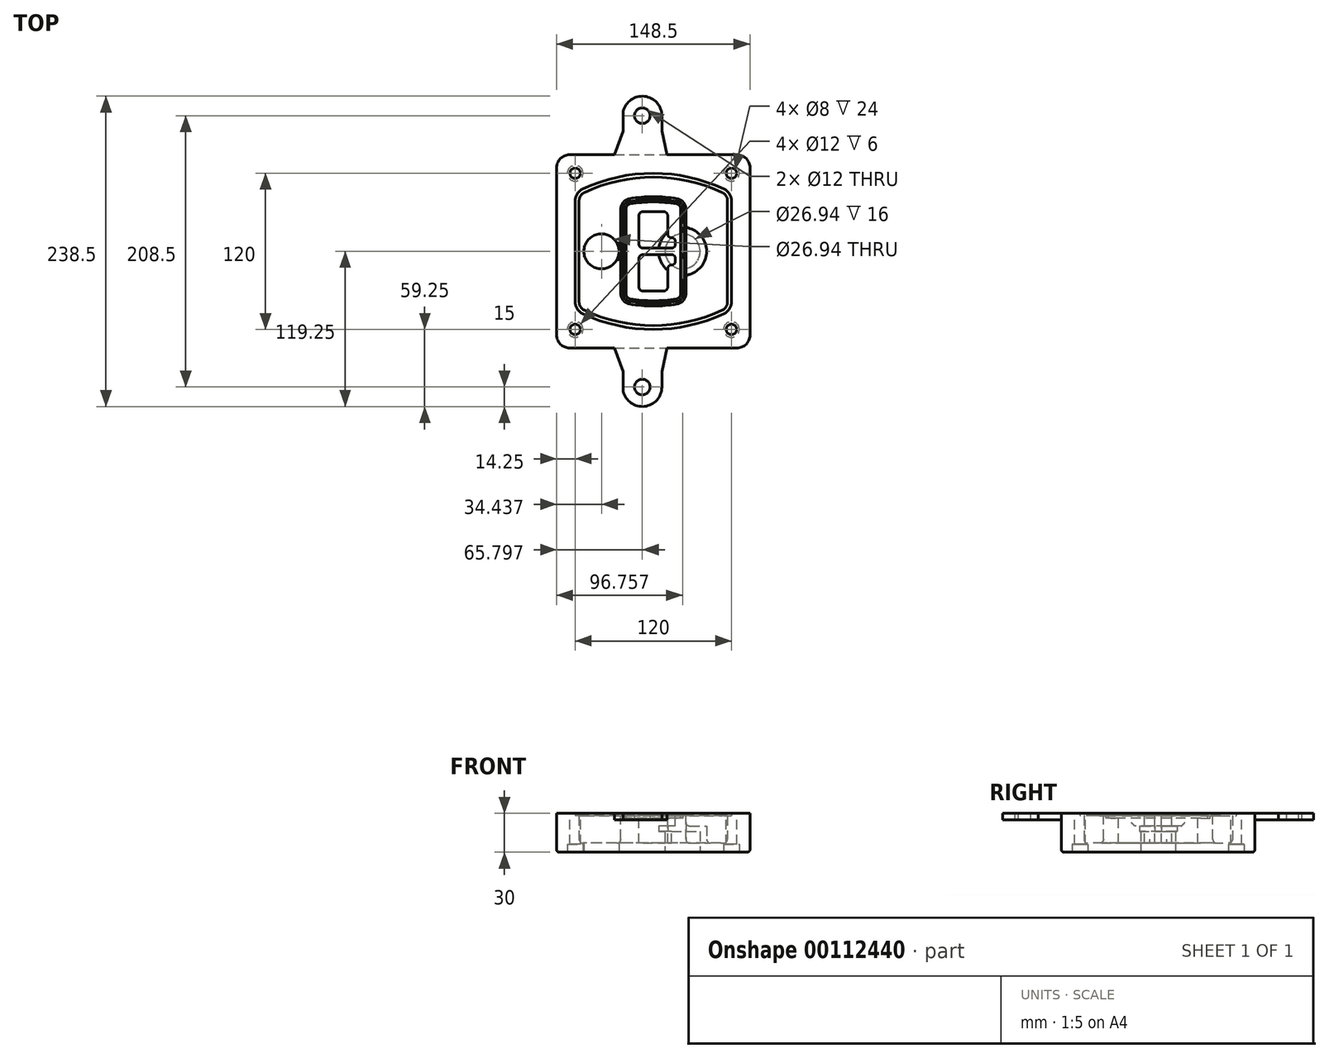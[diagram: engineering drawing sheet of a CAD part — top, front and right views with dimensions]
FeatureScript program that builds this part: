
annotation { "Feature Type Name" : "Feature", "Feature Type Description" : "" }
export const myFeature = defineFeature(function(context is Context, id is Id, definition is map)
    precondition{}
    {
        {
            var Q0;
            Q0=qCreatedBy(makeId("Top.planeOp"),FACE);
            var sketch = newSketch(context, id + "F0", { "sketchPlane" : qUnion([Q0])});
            skPoint(sketch, "E0.rect.middle", {"position": v(0, 0) * mm});
            skLineSegment(sketch, "E1.bottom", {"start": v(-64.25, -74.25) * mm, "end": v(64.25, -74.25) * mm});
            skLineSegment(sketch, "E1.top", {"start": v(-64.25, 74.25) * mm, "end": v(64.25, 74.25) * mm});
            skLineSegment(sketch, "E1.left", {"start": v(-74.25, -64.25) * mm, "end": v(-74.25, 64.25) * mm});
            skLineSegment(sketch, "E1.right", {"start": v(74.25, -64.25) * mm, "end": v(74.25, 64.25) * mm});
            skLineSegment(sketch, "E2", {"start": v(-74.25, 74.25) * mm, "end": v(74.25, -74.25) * mm, "construction": true});
            skLineSegment(sketch, "E3", {"start": v(74.25, 74.25) * mm, "end": v(-74.25, -74.25) * mm, "construction": true});
            skCircle(sketch, "E4", {"center": v(-60, 60) * mm, "radius": 4 * mm});
            skCircle(sketch, "E5", {"center": v(60, 60) * mm, "radius": 4 * mm});
            skCircle(sketch, "E6", {"center": v(60, -60) * mm, "radius": 4 * mm});
            skCircle(sketch, "E7", {"center": v(-60, -60) * mm, "radius": 4 * mm});
            skLineSegment(sketch, "E8", {"start": v(-60, 60) * mm, "end": v(60, 60) * mm, "construction": true});
            skLineSegment(sketch, "E9", {"start": v(60, 60) * mm, "end": v(60, -60) * mm, "construction": true});
            skLineSegment(sketch, "E10", {"start": v(60, -60) * mm, "end": v(-60, -60) * mm, "construction": true});
            skLineSegment(sketch, "E11", {"start": v(-60, -60) * mm, "end": v(-60, 60) * mm, "construction": true});
            skLineSegment(sketch, "E12", {"start": v(-60, 38.83) * mm, "end": v(-60, -38.83) * mm});
            skLineSegment(sketch, "E13", {"start": v(60, 38.83) * mm, "end": v(60, -38.83) * mm});
            skArc(sketch, "E14", {"start": v(54.26, 47.88) * mm, "mid": v(0, 60) * mm, "end": v(-54.26, 47.88) * mm});
            skArc(sketch, "E15", {"start": v(-54.26, -47.88) * mm, "mid": v(0, -60) * mm, "end": v(54.26, -47.88) * mm});
            skLineSegment(sketch, "E16", {"start": v(-60, 0) * mm, "end": v(60, 0) * mm, "construction": true});
            skPoint(sketch, "E17.visualSharp", {"position": v(-60, -45) * mm});
            skArc(sketch, "E17.filletArc", {"start": v(-60, -38.83) * mm, "mid": v(-58.44, -44.2) * mm, "end": v(-54.26, -47.88) * mm});
            skPoint(sketch, "E18.visualSharp", {"position": v(-60, 45) * mm});
            skArc(sketch, "E18.filletArc", {"start": v(-54.26, 47.88) * mm, "mid": v(-58.44, 44.2) * mm, "end": v(-60, 38.83) * mm});
            skPoint(sketch, "E19.visualSharp", {"position": v(60, 45) * mm});
            skArc(sketch, "E19.filletArc", {"start": v(60, 38.83) * mm, "mid": v(58.44, 44.2) * mm, "end": v(54.26, 47.88) * mm});
            skPoint(sketch, "E20.visualSharp", {"position": v(60, -45) * mm});
            skArc(sketch, "E20.filletArc", {"start": v(54.26, -47.88) * mm, "mid": v(58.44, -44.2) * mm, "end": v(60, -38.83) * mm});
            skPoint(sketch, "E21.visualSharp", {"position": v(-74.25, 74.25) * mm});
            skArc(sketch, "E21.filletArc", {"start": v(-64.25, 74.25) * mm, "mid": v(-71.32, 71.32) * mm, "end": v(-74.25, 64.25) * mm});
            skPoint(sketch, "E22.visualSharp", {"position": v(74.25, 74.25) * mm});
            skArc(sketch, "E22.filletArc", {"start": v(74.25, 64.25) * mm, "mid": v(71.32, 71.32) * mm, "end": v(64.25, 74.25) * mm});
            skPoint(sketch, "E23.visualSharp", {"position": v(74.25, -74.25) * mm});
            skArc(sketch, "E23.filletArc", {"start": v(64.25, -74.25) * mm, "mid": v(71.32, -71.32) * mm, "end": v(74.25, -64.25) * mm});
            skPoint(sketch, "E24.visualSharp", {"position": v(-74.25, -74.25) * mm});
            skArc(sketch, "E24.filletArc", {"start": v(-74.25, -64.25) * mm, "mid": v(-71.32, -71.32) * mm, "end": v(-64.25, -74.25) * mm});
            skArc(sketch, "E25.0", {"start": v(57, 38.83) * mm, "mid": v(55.9, 42.58) * mm, "end": v(52.98, 45.17) * mm});
            skLineSegment(sketch, "E25.1", {"start": v(57, 38.83) * mm, "end": v(57, -38.83) * mm});
            skArc(sketch, "E25.2", {"start": v(52.98, -45.17) * mm, "mid": v(55.9, -42.58) * mm, "end": v(57, -38.83) * mm});
            skArc(sketch, "E25.3", {"start": v(-52.98, -45.17) * mm, "mid": v(0, -57) * mm, "end": v(52.98, -45.17) * mm});
            skArc(sketch, "E25.4", {"start": v(-57, -38.83) * mm, "mid": v(-55.9, -42.58) * mm, "end": v(-52.98, -45.17) * mm});
            skArc(sketch, "E25.5", {"start": v(52.98, 45.17) * mm, "mid": v(0, 57) * mm, "end": v(-52.98, 45.17) * mm});
            skLineSegment(sketch, "E25.6", {"start": v(-57, 38.83) * mm, "end": v(-57, -38.83) * mm});
            skArc(sketch, "E25.7", {"start": v(-52.98, 45.17) * mm, "mid": v(-55.9, 42.58) * mm, "end": v(-57, 38.83) * mm});
            skArc(sketch, "E26.0", {"start": v(-55.96, 51.5) * mm, "mid": v(-61.82, 46.33) * mm, "end": v(-64, 38.83) * mm});
            skArc(sketch, "E26.1", {"start": v(55.96, 51.5) * mm, "mid": v(0, 64) * mm, "end": v(-55.96, 51.5) * mm});
            skArc(sketch, "E26.2", {"start": v(64, 38.83) * mm, "mid": v(61.82, 46.33) * mm, "end": v(55.96, 51.5) * mm});
            skLineSegment(sketch, "E26.3", {"start": v(64, 38.83) * mm, "end": v(64, -38.83) * mm});
            skArc(sketch, "E26.4", {"start": v(55.96, -51.5) * mm, "mid": v(61.82, -46.33) * mm, "end": v(64, -38.83) * mm});
            skLineSegment(sketch, "E26.5", {"start": v(-64, 38.83) * mm, "end": v(-64, -38.83) * mm});
            skArc(sketch, "E26.6", {"start": v(-55.96, -51.5) * mm, "mid": v(0, -64) * mm, "end": v(55.96, -51.5) * mm});
            skArc(sketch, "E26.7", {"start": v(-64, -38.83) * mm, "mid": v(-61.82, -46.33) * mm, "end": v(-55.96, -51.5) * mm});
            skSolve(sketch);
        }
        {
            var Q0;
            Q0=makeQuery(id+"F0.imprint","IMPRINT",FACE,{"disambiguationData":[TD([[makeQuery(id+"F0.imprint","IMPRINT",EDGE,{"derivedFrom":sQuery(id+"F0.wireOp",EDGE,"E1.bottom")}),1.0]])]});
            var Q1;
            Q1=makeQuery(id+"F0.imprint","IMPRINT",FACE,{"disambiguationData":[TD([[makeQuery(id+"F0.imprint","IMPRINT",EDGE,{"derivedFrom":sQuery(id+"F0.wireOp",EDGE,"E12")}),1.0]])]});
            var Q2;
            Q2=makeQuery(id+"F0.imprint","IMPRINT",FACE,{"disambiguationData":[TD([[makeQuery(id+"F0.imprint","IMPRINT",EDGE,{"derivedFrom":sQuery(id+"F0.wireOp",EDGE,"E25.0")}),1.0]])]});
            var Q3;
            Q3=makeQuery(id+"F0.imprint","IMPRINT",FACE,{"disambiguationData":[TD([[makeQuery(id+"F0.imprint","IMPRINT",EDGE,{"derivedFrom":sQuery(id+"F0.wireOp",EDGE,"E12")}),-1.0]])]});
            extrude(context, id + "F1", {"entities" : qUnion([Q0, Q1, Q2, Q3]), "oppositeDirection" : true, "depth" : 25 * mm});
        }
        {
            var Q0;
            Q0=makeQuery(id+"F0.imprint","IMPRINT",FACE,{"disambiguationData":[TD([[makeQuery(id+"F0.imprint","IMPRINT",EDGE,{"derivedFrom":sQuery(id+"F0.wireOp",EDGE,"E12")}),1.0]])]});
            extrude(context, id + "F2", {"entities" : qUnion([Q0]), "operationType" : NewBodyOperationType.ADD, "depth" : 3 * mm});
        }
        {
            var Q0;
            Q0=makeQuery(id+"F0.imprint","IMPRINT",FACE,{"disambiguationData":[TD([[makeQuery(id+"F0.imprint","IMPRINT",EDGE,{"derivedFrom":sQuery(id+"F0.wireOp",EDGE,"E25.0")}),1.0]])]});
            extrude(context, id + "F3", {"entities" : qUnion([Q0]), "operationType" : NewBodyOperationType.REMOVE, "oppositeDirection" : true, "depth" : 18 * mm});
        }
        {
            var Q0;
            Q0=makeQuery(id+"F2.opExtrude","CAP_FACE",FACE,{"disambiguationData":[OSD([sQuery(id+"F0.wireOp",EDGE,"E12"),sQuery(id+"F0.wireOp",EDGE,"E13"),sQuery(id+"F0.wireOp",EDGE,"E14"),sQuery(id+"F0.wireOp",EDGE,"E15"),sQuery(id+"F0.wireOp",EDGE,"E17.filletArc"),sQuery(id+"F0.wireOp",EDGE,"E18.filletArc"),sQuery(id+"F0.wireOp",EDGE,"E19.filletArc"),sQuery(id+"F0.wireOp",EDGE,"E20.filletArc"),sQuery(id+"F0.wireOp",EDGE,"E25.0"),sQuery(id+"F0.wireOp",EDGE,"E25.1"),sQuery(id+"F0.wireOp",EDGE,"E25.2"),sQuery(id+"F0.wireOp",EDGE,"E25.3"),sQuery(id+"F0.wireOp",EDGE,"E25.4"),sQuery(id+"F0.wireOp",EDGE,"E25.5"),sQuery(id+"F0.wireOp",EDGE,"E25.6"),sQuery(id+"F0.wireOp",EDGE,"E25.7")])],"isStart":false});
            var sketch = newSketch(context, id + "F4", { "sketchPlane" : qUnion([Q0])});
            skArc(sketch, "E27.0", {"start": v(-18.34, -40.45) * mm, "mid": v(0, -42) * mm, "end": v(18.34, -40.45) * mm});
            skArc(sketch, "E28.0", {"start": v(18.34, 40.45) * mm, "mid": v(0, 42) * mm, "end": v(-18.34, 40.45) * mm});
            skLineSegment(sketch, "E29", {"start": v(-25, 32.57) * mm, "end": v(-25, -32.57) * mm});
            skLineSegment(sketch, "E30", {"start": v(25, 32.57) * mm, "end": v(25, -32.57) * mm});
            skLineSegment(sketch, "E31", {"start": v(-25, 39.1) * mm, "end": v(25, 39.1) * mm, "construction": true});
            skLineSegment(sketch, "E32", {"start": v(-25, -39.1) * mm, "end": v(25, -39.1) * mm, "construction": true});
            skPoint(sketch, "E33.visualSharp", {"position": v(-25, 39.1) * mm});
            skArc(sketch, "E33.filletArc", {"start": v(-18.34, 40.45) * mm, "mid": v(-23.11, 37.73) * mm, "end": v(-25, 32.57) * mm});
            skPoint(sketch, "E34.visualSharp", {"position": v(25, 39.1) * mm});
            skArc(sketch, "E34.filletArc", {"start": v(25, 32.57) * mm, "mid": v(23.11, 37.73) * mm, "end": v(18.34, 40.45) * mm});
            skPoint(sketch, "E35.visualSharp", {"position": v(25, -39.1) * mm});
            skArc(sketch, "E35.filletArc", {"start": v(18.34, -40.45) * mm, "mid": v(23.11, -37.73) * mm, "end": v(25, -32.57) * mm});
            skPoint(sketch, "E36.visualSharp", {"position": v(-25, -39.1) * mm});
            skArc(sketch, "E36.filletArc", {"start": v(-25, -32.57) * mm, "mid": v(-23.11, -37.73) * mm, "end": v(-18.34, -40.45) * mm});
            skArc(sketch, "E37.0", {"start": v(52.98, 45.17) * mm, "mid": v(0, 57) * mm, "end": v(-52.98, 45.17) * mm});
            skArc(sketch, "E37.1", {"start": v(-52.98, 45.17) * mm, "mid": v(-55.9, 42.58) * mm, "end": v(-57, 38.83) * mm});
            skLineSegment(sketch, "E37.2", {"start": v(-57, 38.83) * mm, "end": v(-57, -38.83) * mm});
            skArc(sketch, "E37.3", {"start": v(-57, -38.83) * mm, "mid": v(-55.9, -42.58) * mm, "end": v(-52.98, -45.17) * mm});
            skArc(sketch, "E37.4", {"start": v(-52.98, -45.17) * mm, "mid": v(0, -57) * mm, "end": v(52.98, -45.17) * mm});
            skArc(sketch, "E37.5", {"start": v(52.98, -45.17) * mm, "mid": v(55.9, -42.58) * mm, "end": v(57, -38.83) * mm});
            skLineSegment(sketch, "E37.6", {"start": v(57, 38.83) * mm, "end": v(57, -38.83) * mm});
            skArc(sketch, "E37.7", {"start": v(57, 38.83) * mm, "mid": v(55.9, 42.58) * mm, "end": v(52.98, 45.17) * mm});
            skLineSegment(sketch, "E38.0", {"start": v(23, 32.57) * mm, "end": v(23, -32.57) * mm});
            skArc(sketch, "E38.1", {"start": v(18, -38.48) * mm, "mid": v(21.58, -36.44) * mm, "end": v(23, -32.57) * mm});
            skArc(sketch, "E38.2", {"start": v(-18, -38.48) * mm, "mid": v(0, -40) * mm, "end": v(18, -38.48) * mm});
            skArc(sketch, "E38.3", {"start": v(-23, -32.57) * mm, "mid": v(-21.58, -36.44) * mm, "end": v(-18, -38.48) * mm});
            skLineSegment(sketch, "E38.4", {"start": v(-23, 32.57) * mm, "end": v(-23, -32.57) * mm});
            skArc(sketch, "E38.5", {"start": v(23, 32.57) * mm, "mid": v(21.58, 36.44) * mm, "end": v(18, 38.48) * mm});
            skArc(sketch, "E38.6", {"start": v(-18, 38.48) * mm, "mid": v(-21.58, 36.44) * mm, "end": v(-23, 32.57) * mm});
            skArc(sketch, "E38.7", {"start": v(18, 38.48) * mm, "mid": v(0, 40) * mm, "end": v(-18, 38.48) * mm});
            skArc(sketch, "E39.0", {"start": v(21, 32.57) * mm, "mid": v(20.06, 35.15) * mm, "end": v(17.67, 36.5) * mm});
            skLineSegment(sketch, "E39.1", {"start": v(21, 32.57) * mm, "end": v(21, -32.57) * mm});
            skArc(sketch, "E39.2", {"start": v(17.67, -36.5) * mm, "mid": v(20.06, -35.15) * mm, "end": v(21, -32.57) * mm});
            skArc(sketch, "E39.3", {"start": v(-17.67, -36.5) * mm, "mid": v(0, -38) * mm, "end": v(17.67, -36.5) * mm});
            skArc(sketch, "E39.4", {"start": v(-21, -32.57) * mm, "mid": v(-20.06, -35.15) * mm, "end": v(-17.67, -36.5) * mm});
            skArc(sketch, "E39.5", {"start": v(17.67, 36.5) * mm, "mid": v(0, 38) * mm, "end": v(-17.67, 36.5) * mm});
            skLineSegment(sketch, "E39.6", {"start": v(-21, 32.57) * mm, "end": v(-21, -32.57) * mm});
            skArc(sketch, "E39.7", {"start": v(-17.67, 36.5) * mm, "mid": v(-20.06, 35.15) * mm, "end": v(-21, 32.57) * mm});
            skLineSegment(sketch, "E40", {"start": v(-25, 0) * mm, "end": v(25, 0) * mm, "construction": true});
            skLineSegment(sketch, "E41", {"start": v(-11, 5.5) * mm, "end": v(-11, 27.5) * mm});
            skLineSegment(sketch, "E42", {"start": v(-8, 30.5) * mm, "end": v(8, 30.5) * mm});
            skLineSegment(sketch, "E43", {"start": v(11, 27.5) * mm, "end": v(11, 13.5) * mm});
            skLineSegment(sketch, "E44", {"start": v(14, 10.5) * mm, "end": v(14, 10.5) * mm});
            skLineSegment(sketch, "E45", {"start": v(17, 7.5) * mm, "end": v(17, 5.5) * mm});
            skLineSegment(sketch, "E46", {"start": v(14, 2.5) * mm, "end": v(-8, 2.5) * mm});
            skPoint(sketch, "E47.visualSharp", {"position": v(-11, 30.5) * mm});
            skArc(sketch, "E47.filletArc", {"start": v(-8, 30.5) * mm, "mid": v(-10.12, 29.62) * mm, "end": v(-11, 27.5) * mm});
            skPoint(sketch, "E48.visualSharp", {"position": v(11, 30.5) * mm});
            skArc(sketch, "E48.filletArc", {"start": v(11, 27.5) * mm, "mid": v(10.12, 29.62) * mm, "end": v(8, 30.5) * mm});
            skPoint(sketch, "E49.visualSharp", {"position": v(11, 10.5) * mm});
            skArc(sketch, "E49.filletArc", {"start": v(11, 13.5) * mm, "mid": v(11.88, 11.38) * mm, "end": v(14, 10.5) * mm});
            skPoint(sketch, "E50.visualSharp", {"position": v(17, 10.5) * mm});
            skArc(sketch, "E50.filletArc", {"start": v(17, 7.5) * mm, "mid": v(16.12, 9.62) * mm, "end": v(14, 10.5) * mm});
            skPoint(sketch, "E51.visualSharp", {"position": v(17, 2.5) * mm});
            skArc(sketch, "E51.filletArc", {"start": v(14, 2.5) * mm, "mid": v(16.12, 3.38) * mm, "end": v(17, 5.5) * mm});
            skPoint(sketch, "E52.visualSharp", {"position": v(-11, 2.5) * mm});
            skArc(sketch, "E52.filletArc", {"start": v(-11, 5.5) * mm, "mid": v(-10.12, 3.38) * mm, "end": v(-8, 2.5) * mm});
            skLineSegment(sketch, "E53.0.MirrorCS", {"start": v(14, -2.5) * mm, "end": v(-8, -2.5) * mm});
            skArc(sketch, "E54.0.MirrorCS", {"start": v(-11, -5.5) * mm, "mid": v(-10.12, -3.38) * mm, "end": v(-8, -2.5) * mm});
            skLineSegment(sketch, "E55.0.MirrorCS", {"start": v(-11, -5.5) * mm, "end": v(-11, -27.5) * mm});
            skArc(sketch, "E56.0.MirrorCS", {"start": v(-8, -30.5) * mm, "mid": v(-10.12, -29.62) * mm, "end": v(-11, -27.5) * mm});
            skLineSegment(sketch, "E57.0.MirrorCS", {"start": v(-8, -30.5) * mm, "end": v(8, -30.5) * mm});
            skArc(sketch, "E58.0.MirrorCS", {"start": v(11, -27.5) * mm, "mid": v(10.12, -29.62) * mm, "end": v(8, -30.5) * mm});
            skLineSegment(sketch, "E59.0.MirrorCS", {"start": v(11, -27.5) * mm, "end": v(11, -13.5) * mm});
            skArc(sketch, "E60.0.MirrorCS", {"start": v(11, -13.5) * mm, "mid": v(11.88, -11.38) * mm, "end": v(14, -10.5) * mm});
            skArc(sketch, "E61.0.MirrorCS", {"start": v(17, -7.5) * mm, "mid": v(16.12, -9.62) * mm, "end": v(14, -10.5) * mm});
            skLineSegment(sketch, "E62.0.MirrorCS", {"start": v(17, -7.5) * mm, "end": v(17, -5.5) * mm});
            skArc(sketch, "E63.0.MirrorCS", {"start": v(14, -2.5) * mm, "mid": v(16.12, -3.38) * mm, "end": v(17, -5.5) * mm});
            skSolve(sketch);
        }
        {
            var Q0;
            Q0=makeQuery(id+"F4.imprint","IMPRINT",FACE,{"disambiguationData":[TD([[makeQuery(id+"F4.imprint","IMPRINT",EDGE,{"derivedFrom":sQuery(id+"F4.wireOp",EDGE,"E27.0")}),1.0]])]});
            var Q1;
            Q1=makeQuery(id+"F4.imprint","IMPRINT",FACE,{"disambiguationData":[TD([[makeQuery(id+"F4.imprint","IMPRINT",EDGE,{"derivedFrom":sQuery(id+"F4.wireOp",EDGE,"E38.0")}),-1.0]])]});
            var Q2;
            Q2=makeQuery(id+"F4.imprint","IMPRINT",FACE,{"disambiguationData":[TD([[makeQuery(id+"F4.imprint","IMPRINT",EDGE,{"derivedFrom":sQuery(id+"F4.wireOp",EDGE,"E39.0")}),1.0]])]});
            extrude(context, id + "F5", {"entities" : qUnion([Q0, Q1, Q2]), "operationType" : NewBodyOperationType.ADD, "endBound" : BoundingType.UP_TO_NEXT, "oppositeDirection" : true, "depth" : 25 * mm});
        }
        {
            var Q0;
            Q0=makeQuery(id+"F4.imprint","IMPRINT",FACE,{"disambiguationData":[TD([[makeQuery(id+"F4.imprint","IMPRINT",EDGE,{"derivedFrom":sQuery(id+"F4.wireOp",EDGE,"E38.0")}),-1.0]])]});
            extrude(context, id + "F6", {"entities" : qUnion([Q0]), "operationType" : NewBodyOperationType.REMOVE, "oppositeDirection" : true, "depth" : 2 * mm});
        }
        {
            var Q0;
            Q0=makeQuery(id+"F1.opExtrude","CAP_FACE",FACE,{"disambiguationData":[OSD([sQuery(id+"F0.wireOp",EDGE,"E1.bottom"),sQuery(id+"F0.wireOp",EDGE,"E1.top"),sQuery(id+"F0.wireOp",EDGE,"E1.left"),sQuery(id+"F0.wireOp",EDGE,"E1.right"),sQuery(id+"F0.wireOp",EDGE,"E4"),sQuery(id+"F0.wireOp",EDGE,"E5"),sQuery(id+"F0.wireOp",EDGE,"E6"),sQuery(id+"F0.wireOp",EDGE,"E7"),sQuery(id+"F0.wireOp",EDGE,"E21.filletArc"),sQuery(id+"F0.wireOp",EDGE,"E22.filletArc"),sQuery(id+"F0.wireOp",EDGE,"E23.filletArc"),sQuery(id+"F0.wireOp",EDGE,"E24.filletArc")])],"isStart":false});
            var sketch = newSketch(context, id + "F7", { "sketchPlane" : qUnion([Q0])});
            skCircle(sketch, "E64", {"center": v(22.5, 0) * mm, "radius": 13.47 * mm});
            skCircle(sketch, "E65", {"center": v(-39.81, 0) * mm, "radius": 13.47 * mm});
            skLineSegment(sketch, "E66", {"start": v(74.25, 0) * mm, "end": v(-74.25, 0) * mm});
            skCircle(sketch, "E67", {"center": v(22.5, 0) * mm, "radius": 18.47 * mm});
            skCircle(sketch, "E68", {"center": v(60, -60) * mm, "radius": 6 * mm});
            skCircle(sketch, "E69", {"center": v(-60, -60) * mm, "radius": 6 * mm});
            skCircle(sketch, "E70", {"center": v(-60, 60) * mm, "radius": 6 * mm});
            skCircle(sketch, "E71", {"center": v(60, 60) * mm, "radius": 6 * mm});
            skSolve(sketch);
        }
        {
            var Q0;
            {var subQ1=sQuery(id+"F7.wireOp",EDGE,"E66");var subQ4=sQuery(id+"F7.wireOp",EDGE,"E64");var subQ6=makeQuery(id+"F7.imprint","INTERSECT",VERTEX,{"disambiguationData":[OD(0.0)],"derivedFrom":[subQ4,subQ1]});Q0=makeQuery(id+"F7.imprint","IMPRINT",FACE,{"disambiguationData":[TD([[makeQuery(id+"F7.imprint","IMPRINT",EDGE,{"disambiguationData":[TD([[subQ6,-1.0]])],"derivedFrom":subQ4}),-1.0]])]});}
            var Q1;
            {var subQ0=sQuery(id+"F7.wireOp",EDGE,"E66");var subQ1=sQuery(id+"F7.wireOp",EDGE,"E64");var subQ3=makeQuery(id+"F7.imprint","INTERSECT",VERTEX,{"disambiguationData":[OD(0.0)],"derivedFrom":[subQ1,subQ0]});Q1=makeQuery(id+"F7.imprint","IMPRINT",FACE,{"disambiguationData":[TD([[makeQuery(id+"F7.imprint","IMPRINT",EDGE,{"disambiguationData":[TD([[subQ3,-1.0]])],"derivedFrom":subQ1}),1.0]])]});}
            var Q2;
            {var subQ0=sQuery(id+"F7.wireOp",EDGE,"E66");var subQ1=sQuery(id+"F7.wireOp",EDGE,"E64");var subQ3=makeQuery(id+"F7.imprint","INTERSECT",VERTEX,{"disambiguationData":[OD(0.0)],"derivedFrom":[subQ1,subQ0]});Q2=makeQuery(id+"F7.imprint","IMPRINT",FACE,{"disambiguationData":[TD([[makeQuery(id+"F7.imprint","IMPRINT",EDGE,{"disambiguationData":[TD([[subQ3,1.0]])],"derivedFrom":subQ1}),1.0]])]});}
            var Q3;
            {var subQ1=sQuery(id+"F7.wireOp",EDGE,"E66");var subQ4=sQuery(id+"F7.wireOp",EDGE,"E64");var subQ6=makeQuery(id+"F7.imprint","INTERSECT",VERTEX,{"disambiguationData":[OD(0.0)],"derivedFrom":[subQ4,subQ1]});Q3=makeQuery(id+"F7.imprint","IMPRINT",FACE,{"disambiguationData":[TD([[makeQuery(id+"F7.imprint","IMPRINT",EDGE,{"disambiguationData":[TD([[subQ6,1.0]])],"derivedFrom":subQ4}),-1.0]])]});}
            extrude(context, id + "F8", {"entities" : qUnion([Q0, Q1, Q2, Q3]), "operationType" : NewBodyOperationType.ADD, "oppositeDirection" : true, "depth" : 20 * mm});
        }
        {
            var Q0;
            {var subQ0=sQuery(id+"F7.wireOp",EDGE,"E66");var subQ1=sQuery(id+"F7.wireOp",EDGE,"E64");var subQ3=makeQuery(id+"F7.imprint","INTERSECT",VERTEX,{"disambiguationData":[OD(0.0)],"derivedFrom":[subQ1,subQ0]});Q0=makeQuery(id+"F7.imprint","IMPRINT",FACE,{"disambiguationData":[TD([[makeQuery(id+"F7.imprint","IMPRINT",EDGE,{"disambiguationData":[TD([[subQ3,-1.0]])],"derivedFrom":subQ1}),1.0]])]});}
            var Q1;
            {var subQ0=sQuery(id+"F7.wireOp",EDGE,"E66");var subQ1=sQuery(id+"F7.wireOp",EDGE,"E64");var subQ3=makeQuery(id+"F7.imprint","INTERSECT",VERTEX,{"disambiguationData":[OD(0.0)],"derivedFrom":[subQ1,subQ0]});Q1=makeQuery(id+"F7.imprint","IMPRINT",FACE,{"disambiguationData":[TD([[makeQuery(id+"F7.imprint","IMPRINT",EDGE,{"disambiguationData":[TD([[subQ3,1.0]])],"derivedFrom":subQ1}),1.0]])]});}
            extrude(context, id + "F9", {"entities" : qUnion([Q0, Q1]), "operationType" : NewBodyOperationType.REMOVE, "oppositeDirection" : true, "depth" : 16 * mm});
        }
        {
            var Q0;
            {var subQ0=sQuery(id+"F7.wireOp",EDGE,"E66");var subQ1=sQuery(id+"F7.wireOp",EDGE,"E65");var subQ3=makeQuery(id+"F7.imprint","INTERSECT",VERTEX,{"disambiguationData":[OD(0.0)],"derivedFrom":[subQ1,subQ0]});Q0=makeQuery(id+"F7.imprint","IMPRINT",FACE,{"disambiguationData":[TD([[makeQuery(id+"F7.imprint","IMPRINT",EDGE,{"disambiguationData":[TD([[subQ3,-1.0]])],"derivedFrom":subQ1}),1.0]])]});}
            var Q1;
            {var subQ0=sQuery(id+"F7.wireOp",EDGE,"E66");var subQ1=sQuery(id+"F7.wireOp",EDGE,"E65");var subQ3=makeQuery(id+"F7.imprint","INTERSECT",VERTEX,{"disambiguationData":[OD(0.0)],"derivedFrom":[subQ1,subQ0]});Q1=makeQuery(id+"F7.imprint","IMPRINT",FACE,{"disambiguationData":[TD([[makeQuery(id+"F7.imprint","IMPRINT",EDGE,{"disambiguationData":[TD([[subQ3,1.0]])],"derivedFrom":subQ1}),1.0]])]});}
            extrude(context, id + "F10", {"entities" : qUnion([Q0, Q1]), "operationType" : NewBodyOperationType.REMOVE, "oppositeDirection" : true, "depth" : 25 * mm});
        }
        {
            var Q0;
            Q0=makeQuery(id+"F7.imprint","IMPRINT",FACE,{"disambiguationData":[TD([[makeQuery(id+"F7.imprint","IMPRINT",EDGE,{"derivedFrom":sQuery(id+"F7.wireOp",EDGE,"E68")}),1.0]])]});
            var Q1;
            Q1=makeQuery(id+"F7.imprint","IMPRINT",FACE,{"disambiguationData":[TD([[makeQuery(id+"F7.imprint","IMPRINT",EDGE,{"derivedFrom":makeQuery(id+"F1.opExtrude","CAP_EDGE",EDGE,{"disambiguationData":[OSD([sQuery(id+"F0.wireOp",EDGE,"E5")])],"isStart":false})}),-1.0]])]});
            var Q2;
            Q2=makeQuery(id+"F7.imprint","IMPRINT",FACE,{"disambiguationData":[TD([[makeQuery(id+"F7.imprint","IMPRINT",EDGE,{"derivedFrom":sQuery(id+"F7.wireOp",EDGE,"E69")}),1.0]])]});
            var Q3;
            Q3=makeQuery(id+"F7.imprint","IMPRINT",FACE,{"disambiguationData":[TD([[makeQuery(id+"F7.imprint","IMPRINT",EDGE,{"derivedFrom":makeQuery(id+"F1.opExtrude","CAP_EDGE",EDGE,{"disambiguationData":[OSD([sQuery(id+"F0.wireOp",EDGE,"E4")])],"isStart":false})}),-1.0]])]});
            var Q4;
            Q4=makeQuery(id+"F7.imprint","IMPRINT",FACE,{"disambiguationData":[TD([[makeQuery(id+"F7.imprint","IMPRINT",EDGE,{"derivedFrom":sQuery(id+"F7.wireOp",EDGE,"E70")}),1.0]])]});
            var Q5;
            Q5=makeQuery(id+"F7.imprint","IMPRINT",FACE,{"disambiguationData":[TD([[makeQuery(id+"F7.imprint","IMPRINT",EDGE,{"derivedFrom":makeQuery(id+"F1.opExtrude","CAP_EDGE",EDGE,{"disambiguationData":[OSD([sQuery(id+"F0.wireOp",EDGE,"E7")])],"isStart":false})}),-1.0]])]});
            var Q6;
            Q6=makeQuery(id+"F7.imprint","IMPRINT",FACE,{"disambiguationData":[TD([[makeQuery(id+"F7.imprint","IMPRINT",EDGE,{"derivedFrom":sQuery(id+"F7.wireOp",EDGE,"E71")}),1.0]])]});
            var Q7;
            Q7=makeQuery(id+"F7.imprint","IMPRINT",FACE,{"disambiguationData":[TD([[makeQuery(id+"F7.imprint","IMPRINT",EDGE,{"derivedFrom":makeQuery(id+"F1.opExtrude","CAP_EDGE",EDGE,{"disambiguationData":[OSD([sQuery(id+"F0.wireOp",EDGE,"E6")])],"isStart":false})}),-1.0]])]});
            extrude(context, id + "F11", {"entities" : qUnion([Q0, Q1, Q2, Q3, Q4, Q5, Q6, Q7]), "operationType" : NewBodyOperationType.REMOVE, "oppositeDirection" : true, "depth" : 6 * mm});
        }
        {
            var Q0;
            Q0=makeQuery(id+"F9.boolean.opBoolean","COPY",FACE,{"derivedFrom":makeQuery(id+"F9.opExtrude","CAP_FACE",FACE,{"disambiguationData":[OSD([sQuery(id+"F7.wireOp",EDGE,"E64")])],"isStart":false})});
            var sketch = newSketch(context, id + "F12", { "sketchPlane" : qUnion([Q0])});
            skArc(sketch, "E72.0", {"start": v(11, 14.45) * mm, "mid": v(6.45, 9.13) * mm, "end": v(4.2, 2.5) * mm});
            skArc(sketch, "E72.1", {"start": v(4.2, -2.5) * mm, "mid": v(6.45, -9.13) * mm, "end": v(11, -14.45) * mm});
            skLineSegment(sketch, "E73", {"start": v(4.2, -2.5) * mm, "end": v(14, -2.5) * mm});
            skLineSegment(sketch, "E74.0", {"start": v(14, 2.5) * mm, "end": v(4.2, 2.5) * mm});
            skArc(sketch, "E74.1", {"start": v(14, 2.5) * mm, "mid": v(16.12, 3.38) * mm, "end": v(17, 5.5) * mm});
            skLineSegment(sketch, "E74.2", {"start": v(17, 7.5) * mm, "end": v(17, 5.5) * mm});
            skArc(sketch, "E74.3", {"start": v(17, 7.5) * mm, "mid": v(16.12, 9.62) * mm, "end": v(14, 10.5) * mm});
            skArc(sketch, "E74.4", {"start": v(11, 13.5) * mm, "mid": v(11.88, 11.38) * mm, "end": v(14, 10.5) * mm});
            skLineSegment(sketch, "E74.5", {"start": v(11, 14.45) * mm, "end": v(11, 13.5) * mm});
            skLineSegment(sketch, "E74.7", {"start": v(14, -2.5) * mm, "end": v(4.2, -2.5) * mm});
            skArc(sketch, "E74.8", {"start": v(14, -2.5) * mm, "mid": v(16.12, -3.38) * mm, "end": v(17, -5.5) * mm});
            skLineSegment(sketch, "E74.9", {"start": v(17, -7.5) * mm, "end": v(17, -5.5) * mm});
            skArc(sketch, "E74.10", {"start": v(17, -7.5) * mm, "mid": v(16.12, -9.62) * mm, "end": v(14, -10.5) * mm});
            skArc(sketch, "E74.11", {"start": v(11, -13.5) * mm, "mid": v(11.88, -11.38) * mm, "end": v(14, -10.5) * mm});
            skLineSegment(sketch, "E74.12", {"start": v(11, -14.45) * mm, "end": v(11, -13.5) * mm});
            skPoint(sketch, "E75.orphan", {"position": v(11, -27.5) * mm});
            skPoint(sketch, "E76.orphan", {"position": v(-8, -2.5) * mm});
            skPoint(sketch, "E77.orphan", {"position": v(-8, 2.5) * mm});
            skPoint(sketch, "E78.orphan", {"position": v(11, 27.5) * mm});
            skSolve(sketch);
        }
        {
            var Q0;
            {var subQ7=sQuery(id+"F12.wireOp",EDGE,"E72.0");var subQ14=sQuery(id+"F12.wireOp",EDGE,"E72.1");var subQ16=sQuery(id+"F12.wireOp",EDGE,"E74.1");var subQ18=sQuery(id+"F12.wireOp",EDGE,"E74.8");Q0=qUnion([makeQuery(id+"F12.imprint","IMPRINT",FACE,{"disambiguationData":[TD([[makeQuery(id+"F12.imprint","IMPRINT",EDGE,{"derivedFrom":subQ7}),1.0]])]}),makeQuery(id+"F12.imprint","IMPRINT",FACE,{"disambiguationData":[TD([[makeQuery(id+"F12.imprint","IMPRINT",EDGE,{"derivedFrom":subQ14}),1.0]])]}),makeQuery(id+"F12.imprint","IMPRINT",FACE,{"disambiguationData":[TD([[makeQuery(id+"F12.imprint","IMPRINT",EDGE,{"derivedFrom":subQ16}),1.0]])]}),makeQuery(id+"F12.imprint","IMPRINT",FACE,{"disambiguationData":[TD([[makeQuery(id+"F12.imprint","IMPRINT",EDGE,{"derivedFrom":subQ18}),-1.0]])]})]);}
            var Q1;
            Q1=makeQuery(id+"F5.boolean.opBoolean","SPLIT",FACE,{"disambiguationData":[TD([makeQuery(id+"F5.opExtrude","SWEPT_FACE",FACE,{"disambiguationData":[OSD([sQuery(id+"F4.wireOp",EDGE,"E41")])]})])],"derivedFrom":makeQuery(id+"F3.boolean.opBoolean","COPY",FACE,{"derivedFrom":makeQuery(id+"F3.opExtrude","CAP_FACE",FACE,{"disambiguationData":[OSD([sQuery(id+"F0.wireOp",EDGE,"E25.0"),sQuery(id+"F0.wireOp",EDGE,"E25.1"),sQuery(id+"F0.wireOp",EDGE,"E25.2"),sQuery(id+"F0.wireOp",EDGE,"E25.3"),sQuery(id+"F0.wireOp",EDGE,"E25.4"),sQuery(id+"F0.wireOp",EDGE,"E25.5"),sQuery(id+"F0.wireOp",EDGE,"E25.6"),sQuery(id+"F0.wireOp",EDGE,"E25.7")])],"isStart":false})})});
            extrude(context, id + "F13", {"entities" : qUnion([Q0]), "operationType" : NewBodyOperationType.REMOVE, "endBound" : BoundingType.UP_TO_SURFACE, "endBoundEntityFace" : qUnion([Q1]), "depth" : 25 * mm});
        }
        {
            var Q0;
            Q0=makeQuery(id+"F3.boolean.opBoolean","COPY",EDGE,{"derivedFrom":makeQuery(id+"F3.opExtrude","CAP_EDGE",EDGE,{"disambiguationData":[OSD([sQuery(id+"F0.wireOp",EDGE,"E25.6")])],"isStart":false})});
            var Q1;
            Q1=makeQuery(id+"F8.boolean.opBoolean","INTERSECT",EDGE,{"derivedFrom":[makeQuery(id+"F5.opExtrude","SWEPT_FACE",FACE,{"disambiguationData":[OSD([sQuery(id+"F4.wireOp",EDGE,"E30")])]}),makeQuery(id+"F8.opExtrude","CAP_FACE",FACE,{"disambiguationData":[OSD([sQuery(id+"F7.wireOp",EDGE,"E67")])],"isStart":false})]});
            var Q2;
            Q2=makeQuery(id+"F8.boolean.opBoolean","INTERSECT",EDGE,{"disambiguationData":[OD(1.0)],"derivedFrom":[makeQuery(id+"F5.opExtrude","SWEPT_FACE",FACE,{"disambiguationData":[OSD([sQuery(id+"F4.wireOp",EDGE,"E30")])]}),makeQuery(id+"F8.opExtrude","SWEPT_FACE",FACE,{"disambiguationData":[OSD([sQuery(id+"F7.wireOp",EDGE,"E67")])]})]});
            var Q3;
            {var subQ0=sQuery(id+"F4.wireOp",EDGE,"E30");Q3=makeQuery(id+"F8.boolean.opBoolean","SPLIT",EDGE,{"disambiguationData":[TD([makeQuery(id+"F5.opExtrude","SWEPT_FACE",FACE,{"disambiguationData":[OSD([sQuery(id+"F4.wireOp",EDGE,"E35.filletArc")])]})])],"derivedFrom":makeQuery(id+"F5.opExtrude","CAP_EDGE",EDGE,{"disambiguationData":[OSD([subQ0])],"isStart":false})});}
            var Q4;
            {var subQ0=sQuery(id+"F0.wireOp",EDGE,"E25.7");var subQ1=sQuery(id+"F0.wireOp",EDGE,"E25.1");var subQ2=sQuery(id+"F0.wireOp",EDGE,"E25.6");var subQ3=sQuery(id+"F0.wireOp",EDGE,"E25.5");var subQ4=sQuery(id+"F0.wireOp",EDGE,"E25.4");var subQ5=sQuery(id+"F0.wireOp",EDGE,"E25.0");var subQ6=sQuery(id+"F0.wireOp",EDGE,"E25.2");var subQ7=sQuery(id+"F0.wireOp",EDGE,"E25.3");Q4=makeQuery(id+"F8.boolean.opBoolean","INTERSECT",EDGE,{"derivedFrom":[makeQuery(id+"F5.boolean.opBoolean","SPLIT",FACE,{"disambiguationData":[TD([makeQuery(id+"F2.opExtrude","SWEPT_FACE",FACE,{"disambiguationData":[OSD([subQ5])]})])],"derivedFrom":makeQuery(id+"F3.boolean.opBoolean","COPY",FACE,{"derivedFrom":makeQuery(id+"F3.opExtrude","CAP_FACE",FACE,{"disambiguationData":[OSD([subQ5,subQ1,subQ6,subQ7,subQ4,subQ3,subQ2,subQ0])],"isStart":false})})}),makeQuery(id+"F8.opExtrude","SWEPT_FACE",FACE,{"disambiguationData":[OSD([sQuery(id+"F7.wireOp",EDGE,"E67")])]})]});}
            var Q5;
            Q5=makeQuery(id+"F8.boolean.opBoolean","INTERSECT",EDGE,{"disambiguationData":[OD(0.0)],"derivedFrom":[makeQuery(id+"F5.opExtrude","SWEPT_FACE",FACE,{"disambiguationData":[OSD([sQuery(id+"F4.wireOp",EDGE,"E30")])]}),makeQuery(id+"F8.opExtrude","SWEPT_FACE",FACE,{"disambiguationData":[OSD([sQuery(id+"F7.wireOp",EDGE,"E67")])]})]});
            fillet(context, id + "F14", {"entities" : qUnion([Q0, Q1, Q2, Q3, Q4, Q5]), "radius" : 3 * mm, "tangentPropagation" : true, "allowEdgeOverflow" : false});
        }
        {
            var Q0;
            Q0=makeQuery(id+"F1.opExtrude","CAP_EDGE",EDGE,{"disambiguationData":[OSD([sQuery(id+"F0.wireOp",EDGE,"E1.bottom")])],"isStart":false});
            fillet(context, id + "F15", {"entities" : qUnion([Q0]), "radius" : 2 * mm, "tangentPropagation" : true, "allowEdgeOverflow" : false});
        }
        {
            var Q0;
            {var subQ0=sQuery(id+"F0.wireOp",EDGE,"E22.filletArc");var subQ1=sQuery(id+"F0.wireOp",EDGE,"E7");var subQ2=sQuery(id+"F0.wireOp",EDGE,"E6");var subQ3=sQuery(id+"F0.wireOp",EDGE,"E5");var subQ4=sQuery(id+"F0.wireOp",EDGE,"E4");var subQ5=sQuery(id+"F0.wireOp",EDGE,"E1.bottom");var subQ6=sQuery(id+"F0.wireOp",EDGE,"E21.filletArc");var subQ7=sQuery(id+"F0.wireOp",EDGE,"E1.top");var subQ8=sQuery(id+"F0.wireOp",EDGE,"E1.left");var subQ9=sQuery(id+"F0.wireOp",EDGE,"E1.right");var subQ10=sQuery(id+"F0.wireOp",EDGE,"E23.filletArc");var subQ11=sQuery(id+"F0.wireOp",EDGE,"E24.filletArc");Q0=makeQuery(id+"F2.boolean.opBoolean","SPLIT",FACE,{"disambiguationData":[TD([makeQuery(id+"F1.opExtrude","SWEPT_FACE",FACE,{"disambiguationData":[OSD([subQ5])]})])],"derivedFrom":makeQuery(id+"F1.opExtrude","CAP_FACE",FACE,{"disambiguationData":[OSD([subQ5,subQ7,subQ8,subQ9,subQ4,subQ3,subQ2,subQ1,subQ6,subQ0,subQ10,subQ11])],"isStart":true})});}
            var sketch = newSketch(context, id + "F16", { "sketchPlane" : qUnion([Q0])});
            skLineSegment(sketch, "E79", {"start": v(-29.78, 74.25) * mm, "end": v(-23.06, 92.25) * mm});
            skLineSegment(sketch, "E80", {"start": v(-23.06, 92.25) * mm, "end": v(-23.06, 107.66) * mm});
            skLineSegment(sketch, "E81", {"start": v(10.4, 74.25) * mm, "end": v(6.55, 92.25) * mm});
            skLineSegment(sketch, "E82", {"start": v(6.55, 92.25) * mm, "end": v(6.55, 104.25) * mm});
            skArc(sketch, "E83", {"start": v(6.55, 104.25) * mm, "mid": v(-6.74, 119.15) * mm, "end": v(-23.06, 107.66) * mm});
            skCircle(sketch, "E84", {"center": v(-8.45, 104.25) * mm, "radius": 6 * mm});
            skLineSegment(sketch, "E85", {"start": v(-74.25, 0) * mm, "end": v(74.25, 0) * mm});
            skLineSegment(sketch, "E86.MirrorCS", {"start": v(-29.78, -74.25) * mm, "end": v(-23.06, -92.25) * mm});
            skLineSegment(sketch, "E87.MirrorCS", {"start": v(-23.06, -92.25) * mm, "end": v(-23.06, -107.66) * mm});
            skCircle(sketch, "E88.MirrorC", {"center": v(-8.45, -104.25) * mm, "radius": 6 * mm});
            skArc(sketch, "E89.MirrorCS", {"start": v(6.55, -104.25) * mm, "mid": v(-6.74, -119.15) * mm, "end": v(-23.06, -107.66) * mm});
            skLineSegment(sketch, "E90.MirrorCS", {"start": v(10.4, -74.25) * mm, "end": v(6.55, -92.25) * mm});
            skLineSegment(sketch, "E91.MirrorCS", {"start": v(6.55, -92.25) * mm, "end": v(6.55, -104.25) * mm});
            skSolve(sketch);
        }
        {
            var Q0;
            {var subQ0=sQuery(id+"F16.wireOp",EDGE,"E86.MirrorCS");Q0=makeQuery(id+"F16.imprint","IMPRINT",FACE,{"disambiguationData":[TD([[makeQuery(id+"F16.imprint","IMPRINT",EDGE,{"derivedFrom":subQ0}),1.0]])]});}
            var Q1;
            Q1=makeQuery(id+"F16.imprint","IMPRINT",FACE,{"disambiguationData":[TD([[makeQuery(id+"F16.imprint","IMPRINT",EDGE,{"derivedFrom":makeQuery(id+"F1.opExtrude","CAP_EDGE",EDGE,{"disambiguationData":[OSD([sQuery(id+"F0.wireOp",EDGE,"E6")])],"isStart":true})}),-1.0]])]});
            var Q2;
            Q2=makeQuery(id+"F16.imprint","IMPRINT",FACE,{"disambiguationData":[TD([[makeQuery(id+"F16.imprint","IMPRINT",EDGE,{"derivedFrom":makeQuery(id+"F1.opExtrude","CAP_EDGE",EDGE,{"disambiguationData":[OSD([sQuery(id+"F0.wireOp",EDGE,"E4")])],"isStart":true})}),-1.0]])]});
            var Q3;
            {var subQ1=sQuery(id+"F16.wireOp",EDGE,"E79");Q3=makeQuery(id+"F16.imprint","IMPRINT",FACE,{"disambiguationData":[TD([[makeQuery(id+"F16.imprint","IMPRINT",EDGE,{"derivedFrom":subQ1}),-1.0]])]});}
            extrude(context, id + "F17", {"entities" : qUnion([Q0, Q1, Q2, Q3]), "operationType" : NewBodyOperationType.ADD, "depth" : 5 * mm});
        }
    });
